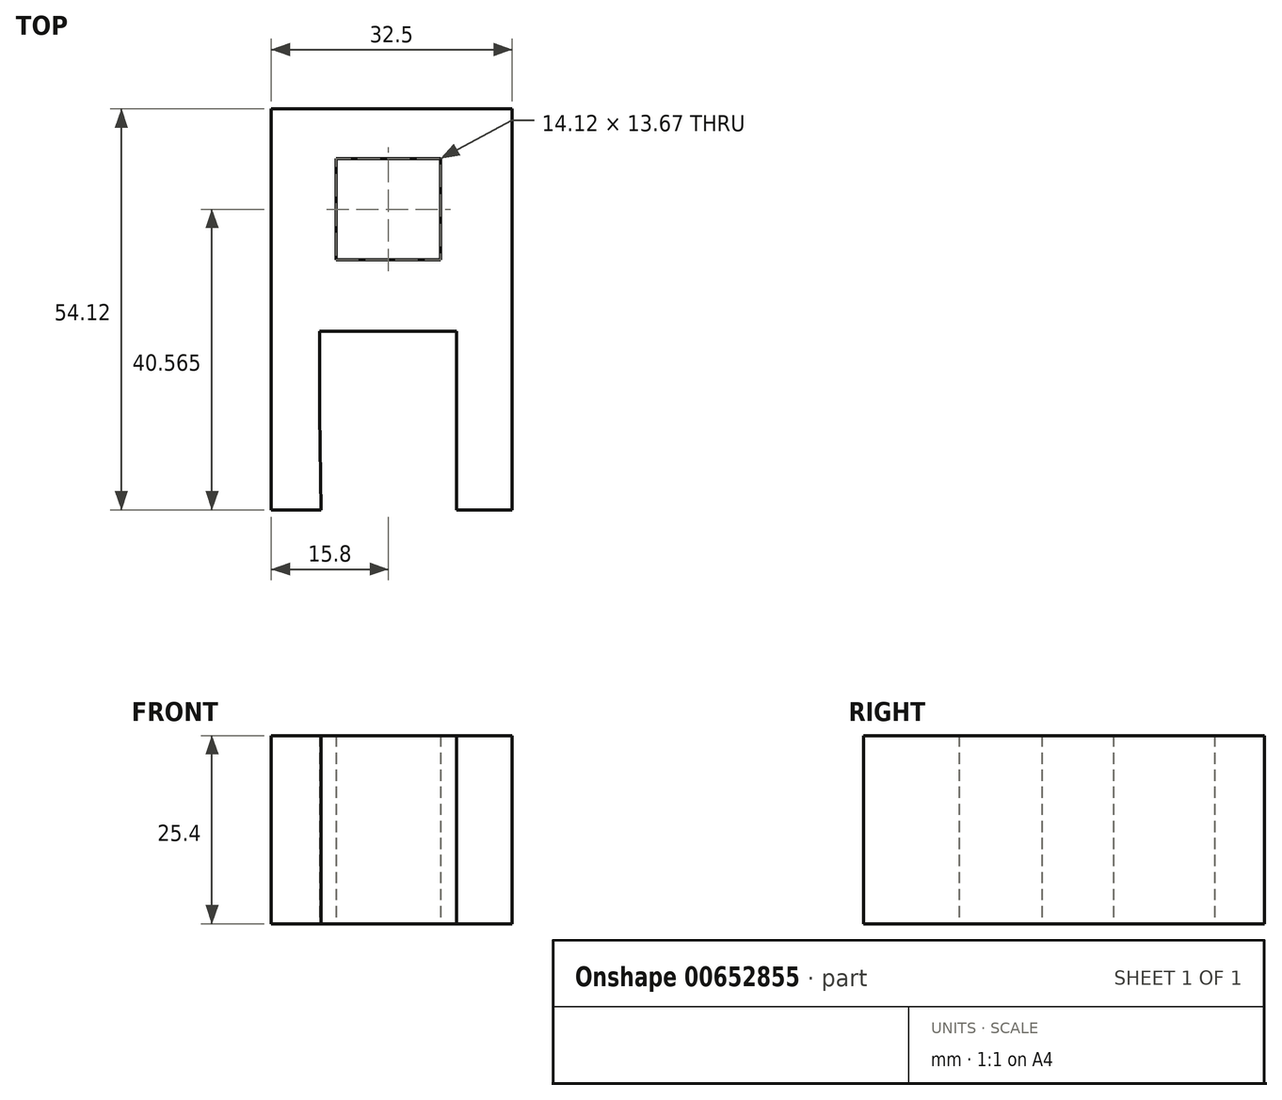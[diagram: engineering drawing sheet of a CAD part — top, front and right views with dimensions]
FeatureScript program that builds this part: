
annotation { "Feature Type Name" : "Feature", "Feature Type Description" : "" }
export const myFeature = defineFeature(function(context is Context, id is Id, definition is map)
    precondition{}
    {
        {
            var Q0;
            Q0=qCreatedBy(makeId("Top.planeOp"),FACE);
            var sketch = newSketch(context, id + "F0", { "sketchPlane" : qUnion([Q0])});
            skLineSegment(sketch, "E0", {"start": v(0, 0) * mm, "end": v(0, 37.68) * mm});
            skLineSegment(sketch, "E1", {"start": v(180.5, -51.44) * mm, "end": v(134.7, 9.3) * mm});
            skLineSegment(sketch, "E2", {"start": v(0, 37.68) * mm, "end": v(0, 54.12) * mm});
            skLineSegment(sketch, "E3", {"start": v(0, 54.12) * mm, "end": v(32.5, 54.12) * mm});
            skLineSegment(sketch, "E4", {"start": v(32.5, 54.12) * mm, "end": v(32.5, 0) * mm});
            skLineSegment(sketch, "E5", {"start": v(0, 37.68) * mm, "end": v(0, 3.92) * mm});
            skLineSegment(sketch, "E6", {"start": v(0, 3.92) * mm, "end": v(0, 0) * mm});
            skLineSegment(sketch, "E7", {"start": v(32.5, 0) * mm, "end": v(25, 0) * mm});
            skLineSegment(sketch, "E8", {"start": v(6.72, 0) * mm, "end": v(6.52, 12.9) * mm});
            skLineSegment(sketch, "E9", {"start": v(6.52, 12.9) * mm, "end": v(6.52, 24.1) * mm});
            skLineSegment(sketch, "E10", {"start": v(6.52, 24.1) * mm, "end": v(15.91, 24.1) * mm});
            skLineSegment(sketch, "E11", {"start": v(25, 1.97) * mm, "end": v(25, 24.1) * mm});
            skLineSegment(sketch, "E12", {"start": v(15.91, 24.1) * mm, "end": v(25, 24.1) * mm});
            skLineSegment(sketch, "E13", {"start": v(8.74, 46.28) * mm, "end": v(8.74, 33.73) * mm});
            skLineSegment(sketch, "E14", {"start": v(8.74, 33.73) * mm, "end": v(15.91, 33.73) * mm});
            skLineSegment(sketch, "E15", {"start": v(15.91, 33.73) * mm, "end": v(22.86, 33.73) * mm});
            skLineSegment(sketch, "E16", {"start": v(22.86, 33.73) * mm, "end": v(22.86, 47.4) * mm});
            skLineSegment(sketch, "E17", {"start": v(22.86, 47.4) * mm, "end": v(8.74, 47.4) * mm});
            skLineSegment(sketch, "E18", {"start": v(8.74, 46.28) * mm, "end": v(8.74, 47.4) * mm});
            skLineSegment(sketch, "E19", {"start": v(25, 1.97) * mm, "end": v(25, 0) * mm});
            skLineSegment(sketch, "E20", {"start": v(0, 0) * mm, "end": v(0, 3.92) * mm});
            skLineSegment(sketch, "E21", {"start": v(0, -0.22) * mm, "end": v(-1.26, -0.22) * mm});
            skLineSegment(sketch, "E22", {"start": v(0, 0) * mm, "end": v(6.72, 0) * mm});
            skLineSegment(sketch, "E23", {"start": v(0, 3.92) * mm, "end": v(0, 1.54) * mm});
            skSolve(sketch);
        }
        {
            var Q0;
            Q0 = qSketchRegion(id + "F0", true);
            extrude(context, id + "F1", {"entities" : qUnion([Q0]), "depth" : 25.4 * mm, "offsetDistance" : 25.4 * mm});
        }
    });
